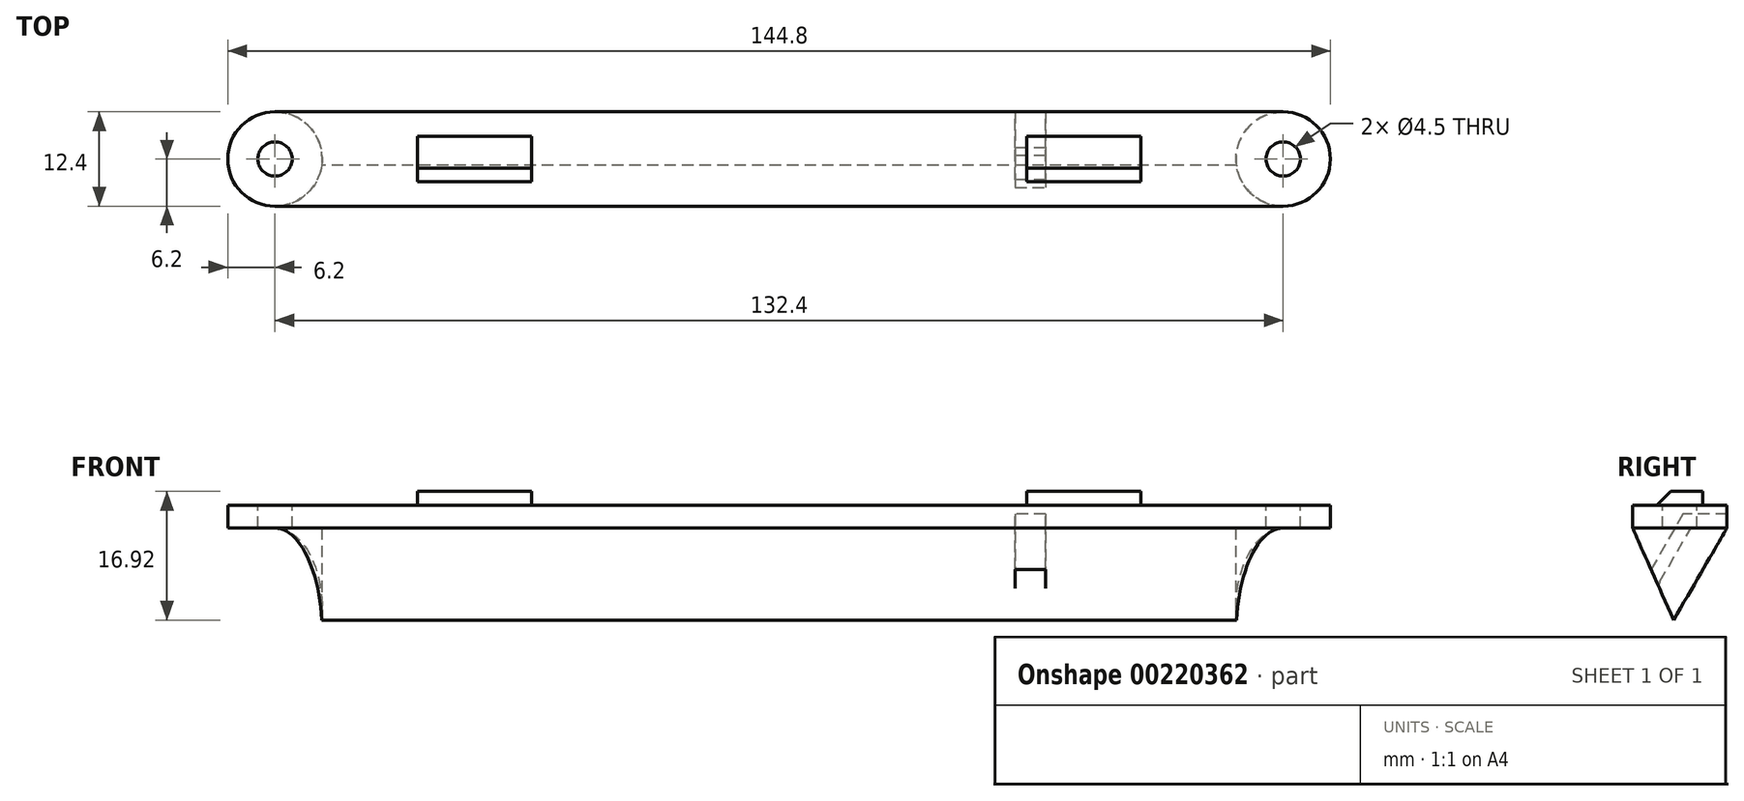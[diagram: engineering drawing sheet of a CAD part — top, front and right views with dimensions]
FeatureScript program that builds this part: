
annotation { "Feature Type Name" : "Feature", "Feature Type Description" : "" }
export const myFeature = defineFeature(function(context is Context, id is Id, definition is map)
    precondition{}
    {
        {
            var Q0;
            Q0=qCreatedBy(makeId("Top.planeOp"),FACE);
            var sketch = newSketch(context, id + "F0", { "sketchPlane" : qUnion([Q0])});
            skCircle(sketch, "E0", {"center": v(66.2, 0) * mm, "radius": 6.2 * mm});
            skCircle(sketch, "E1", {"center": v(-66.2, 0) * mm, "radius": 6.2 * mm});
            skLineSegment(sketch, "E2.bottom", {"start": v(-32.5, 3) * mm, "end": v(-47.5, 3) * mm});
            skLineSegment(sketch, "E2.top", {"start": v(-32.5, -3) * mm, "end": v(-47.5, -3) * mm});
            skLineSegment(sketch, "E2.left", {"start": v(-32.5, 3) * mm, "end": v(-32.5, -3) * mm});
            skLineSegment(sketch, "E2.right", {"start": v(-47.5, 3) * mm, "end": v(-47.5, -3) * mm});
            skPoint(sketch, "E2.middle", {"position": v(-40, 0) * mm});
            skLineSegment(sketch, "E3.bottom", {"start": v(47.5, 3) * mm, "end": v(32.5, 3) * mm});
            skLineSegment(sketch, "E3.top", {"start": v(47.5, -3) * mm, "end": v(32.5, -3) * mm});
            skLineSegment(sketch, "E3.left", {"start": v(47.5, 3) * mm, "end": v(47.5, -3) * mm});
            skLineSegment(sketch, "E3.right", {"start": v(32.5, 3) * mm, "end": v(32.5, -3) * mm});
            skPoint(sketch, "E3.middle", {"position": v(40, 0) * mm});
            skCircle(sketch, "E4", {"center": v(-66.2, 0) * mm, "radius": 2.25 * mm});
            skCircle(sketch, "E5", {"center": v(66.2, 0) * mm, "radius": 2.25 * mm});
            skLineSegment(sketch, "E6", {"start": v(-66.2, 6.2) * mm, "end": v(66.2, 6.2) * mm});
            skLineSegment(sketch, "E7", {"start": v(66.2, -6.2) * mm, "end": v(-66.2, -6.2) * mm});
            skSolve(sketch);
        }
        {
            var Q0;
            Q0=makeQuery(id+"F0.imprint","IMPRINT",FACE,{"disambiguationData":[TD([[makeQuery(id+"F0.imprint","IMPRINT",EDGE,{"derivedFrom":sQuery(id+"F0.wireOp",EDGE,"E2.bottom")}),1.0]])]});
            var Q1;
            Q1=makeQuery(id+"F0.imprint","IMPRINT",FACE,{"disambiguationData":[TD([[makeQuery(id+"F0.imprint","IMPRINT",EDGE,{"derivedFrom":sQuery(id+"F0.wireOp",EDGE,"E3.bottom")}),1.0]])]});
            var Q2;
            Q2=makeQuery(id+"F0.imprint","IMPRINT",FACE,{"disambiguationData":[TD([[makeQuery(id+"F0.imprint","IMPRINT",EDGE,{"derivedFrom":sQuery(id+"F0.wireOp",EDGE,"E2.bottom")}),-1.0]])]});
            extrude(context, id + "F1", {"entities" : qUnion([Q0, Q1, Q2]), "oppositeDirection" : true, "depth" : 30 * mm});
        }
        {
            var Q0;
            Q0=makeQuery(id+"F0.imprint","IMPRINT",FACE,{"disambiguationData":[TD([[makeQuery(id+"F0.imprint","IMPRINT",EDGE,{"derivedFrom":sQuery(id+"F0.wireOp",EDGE,"E2.bottom")}),1.0]])]});
            var Q1;
            Q1=makeQuery(id+"F0.imprint","IMPRINT",FACE,{"disambiguationData":[TD([[makeQuery(id+"F0.imprint","IMPRINT",EDGE,{"derivedFrom":sQuery(id+"F0.wireOp",EDGE,"E3.bottom")}),1.0]])]});
            extrude(context, id + "F2", {"entities" : qUnion([Q0, Q1]), "operationType" : NewBodyOperationType.ADD, "depth" : 1.8 * mm});
        }
        {
            var Q0;
            Q0=makeQuery(id+"F0.imprint","IMPRINT",FACE,{"disambiguationData":[TD([[makeQuery(id+"F0.imprint","IMPRINT",EDGE,{"derivedFrom":sQuery(id+"F0.wireOp",EDGE,"E4")}),-1.0]])]});
            var Q1;
            Q1=makeQuery(id+"F0.imprint","IMPRINT",FACE,{"disambiguationData":[TD([[makeQuery(id+"F0.imprint","IMPRINT",EDGE,{"derivedFrom":sQuery(id+"F0.wireOp",EDGE,"E5")}),-1.0]])]});
            extrude(context, id + "F3", {"entities" : qUnion([Q0, Q1]), "operationType" : NewBodyOperationType.ADD, "oppositeDirection" : true, "depth" : 3 * mm});
        }
        {
            var Q0;
            Q0=makeQuery(id+"F2.opExtrude","CAP_EDGE",EDGE,{"disambiguationData":[OSD([sQuery(id+"F0.wireOp",EDGE,"E3.top")])],"isStart":false});
            var Q1;
            Q1=makeQuery(id+"F2.opExtrude","CAP_EDGE",EDGE,{"disambiguationData":[OSD([sQuery(id+"F0.wireOp",EDGE,"E2.top")])],"isStart":false});
            chamfer(context, id + "F4", {"entities" : qUnion([Q0, Q1]), "width" : 1.8 * mm, "tangentPropagation" : true});
        }
        {
            var Q0;
            Q0=qCreatedBy(makeId("Right.planeOp"),FACE);
            var sketch = newSketch(context, id + "F5", { "sketchPlane" : qUnion([Q0])});
            skLineSegment(sketch, "E8", {"start": v(-6.2, -3) * mm, "end": v(6.2, -3) * mm});
            skLineSegment(sketch, "E9", {"start": v(6.2, -3) * mm, "end": v(-0.8, -15.12) * mm});
            skLineSegment(sketch, "E10", {"start": v(-0.8, -15.12) * mm, "end": v(-6.2, -3) * mm});
            skLineSegment(sketch, "E11", {"start": v(-6.2, -3) * mm, "end": v(-6.2, -30) * mm});
            skLineSegment(sketch, "E12", {"start": v(-6.2, -30) * mm, "end": v(6.2, -30) * mm});
            skLineSegment(sketch, "E13", {"start": v(6.2, -30) * mm, "end": v(6.2, -3) * mm});
            skSolve(sketch);
        }
        {
            var Q0;
            Q0=makeQuery(id+"F5.imprint","IMPRINT",FACE,{"disambiguationData":[TD([[makeQuery(id+"F5.imprint","IMPRINT",EDGE,{"derivedFrom":sQuery(id+"F5.wireOp",EDGE,"E9")}),1.0]])]});
            extrude(context, id + "F6", {"entities" : qUnion([Q0]), "operationType" : NewBodyOperationType.REMOVE, "endBound" : BoundingType.UP_TO_NEXT, "depth" : 120 * mm, "hasSecondDirection" : true, "secondDirectionBound" : SecondDirectionBoundingType.UP_TO_NEXT, "secondDirectionOppositeDirection" : true, "secondDirectionDepth" : 25 * mm});
        }
        {
            var Q0;
            Q0=qCreatedBy(makeId("Right.planeOp"),FACE);
            var sketch = newSketch(context, id + "F7", { "sketchPlane" : qUnion([Q0])});
            skLineSegment(sketch, "E14", {"start": v(6.2, -1.2) * mm, "end": v(0.43, -1.2) * mm});
            skLineSegment(sketch, "E15", {"start": v(0.43, -1.2) * mm, "end": v(-6.2, -12.68) * mm});
            skLineSegment(sketch, "E16", {"start": v(-6.2, -12.68) * mm, "end": v(-6.2, -16.28) * mm});
            skLineSegment(sketch, "E17", {"start": v(-6.2, -16.28) * mm, "end": v(1.47, -3) * mm});
            skLineSegment(sketch, "E18", {"start": v(1.47, -3) * mm, "end": v(6.2, -3) * mm});
            skLineSegment(sketch, "E19", {"start": v(6.2, -3) * mm, "end": v(6.2, -1.2) * mm});
            skSolve(sketch);
        }
        {
            var Q0;
            Q0=makeQuery(id+"F7.imprint","IMPRINT",FACE,{"disambiguationData":[TD([[makeQuery(id+"F7.imprint","IMPRINT",EDGE,{"derivedFrom":sQuery(id+"F7.wireOp",EDGE,"E14")}),1.0]])]});
            extrude(context, id + "F8", {"entities" : qUnion([Q0]), "operationType" : NewBodyOperationType.REMOVE, "depth" : (33 + 2) * mm, "hasSecondDirection" : true, "secondDirectionOppositeDirection" : false, "secondDirectionDepth" : (33 - 2) * mm});
        }
        {
            var Q0;
            Q0=makeQuery(id+"F6.boolean.opBoolean","COPY",EDGE,{"derivedFrom":makeQuery(id+"F6.opExtrude","TWEAK_EDGE",EDGE,{"derivedFrom":[makeQuery(id+"F5.imprint","IMPRINT",EDGE,{"derivedFrom":sQuery(id+"F5.wireOp",EDGE,"E9")}),makeQuery(id+"F5.imprint","IMPRINT",EDGE,{"derivedFrom":sQuery(id+"F5.wireOp",EDGE,"E10")})]})});
            var Q1;
            Q1=makeQuery(id+"F6.boolean.opBoolean","COPY",EDGE,{"derivedFrom":makeQuery(id+"F6.opExtrude","TWEAK_EDGE",EDGE,{"derivedFrom":[makeQuery(id+"F1.opExtrude","SWEPT_FACE",FACE,{"disambiguationData":[OSD([sQuery(id+"F0.wireOp",EDGE,"E1")])]}),makeQuery(id+"F5.imprint","IMPRINT",EDGE,{"derivedFrom":sQuery(id+"F5.wireOp",EDGE,"E9")})]})});
            var Q2;
            Q2=makeQuery(id+"F6.boolean.opBoolean","COPY",EDGE,{"derivedFrom":makeQuery(id+"F6.opExtrude","TWEAK_EDGE",EDGE,{"derivedFrom":[makeQuery(id+"F1.opExtrude","SWEPT_FACE",FACE,{"disambiguationData":[OSD([sQuery(id+"F0.wireOp",EDGE,"E1")])]}),makeQuery(id+"F5.imprint","IMPRINT",EDGE,{"derivedFrom":sQuery(id+"F5.wireOp",EDGE,"E10")})]})});
            var Q3;
            Q3=makeQuery(id+"F6.boolean.opBoolean","COPY",EDGE,{"derivedFrom":makeQuery(id+"F6.opExtrude","TWEAK_EDGE",EDGE,{"derivedFrom":[makeQuery(id+"F1.opExtrude","SWEPT_FACE",FACE,{"disambiguationData":[OSD([sQuery(id+"F0.wireOp",EDGE,"E0")])]}),makeQuery(id+"F5.imprint","IMPRINT",EDGE,{"derivedFrom":sQuery(id+"F5.wireOp",EDGE,"E10")})]})});
            var Q4;
            Q4=makeQuery(id+"F6.boolean.opBoolean","COPY",EDGE,{"derivedFrom":makeQuery(id+"F6.opExtrude","TWEAK_EDGE",EDGE,{"derivedFrom":[makeQuery(id+"F1.opExtrude","SWEPT_FACE",FACE,{"disambiguationData":[OSD([sQuery(id+"F0.wireOp",EDGE,"E0")])]}),makeQuery(id+"F5.imprint","IMPRINT",EDGE,{"derivedFrom":sQuery(id+"F5.wireOp",EDGE,"E9")})]})});
            var Q5;
            Q5=makeQuery(id+"Fy0fjpXj2qNrPrX_1.1.F8.boolean.opBoolean","INTERSECT",EDGE,{"derivedFrom":[makeQuery(id+"F6.boolean.opBoolean","COPY",FACE,{"derivedFrom":makeQuery(id+"F6.opExtrude","SWEPT_FACE",FACE,{"disambiguationData":[OSD([sQuery(id+"F5.wireOp",EDGE,"E10")])]})}),makeQuery(id+"Fy0fjpXj2qNrPrX_1.1.F8.opExtrude","SWEPT_FACE",FACE,{"disambiguationData":[OSD([sQuery(id+"F7.wireOp",EDGE,"E17")])]})]});
            var Q6;
            Q6=makeQuery(id+"F8.boolean.opBoolean","INTERSECT",EDGE,{"derivedFrom":[makeQuery(id+"F6.boolean.opBoolean","COPY",FACE,{"derivedFrom":makeQuery(id+"F6.opExtrude","SWEPT_FACE",FACE,{"disambiguationData":[OSD([sQuery(id+"F5.wireOp",EDGE,"E10")])]})}),makeQuery(id+"F8.opExtrude","SWEPT_FACE",FACE,{"disambiguationData":[OSD([sQuery(id+"F7.wireOp",EDGE,"E17")])]})]});
            fillet(context, id + "F9", {"entities" : qUnion([Q0, Q1, Q2, Q3, Q4, Q5, Q6]), "radius" : 1 * mm, "tangentPropagation" : true, "allowEdgeOverflow" : false});
        }
    });
